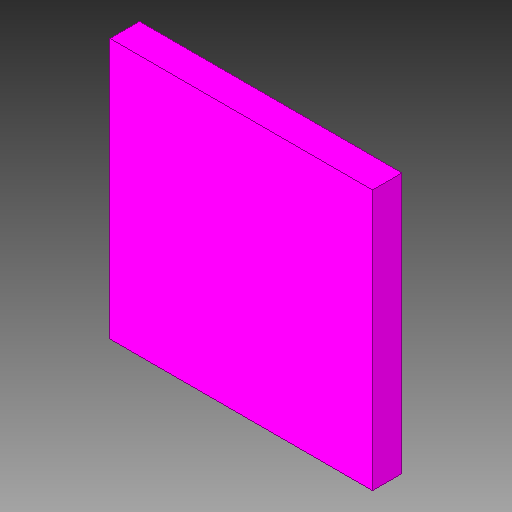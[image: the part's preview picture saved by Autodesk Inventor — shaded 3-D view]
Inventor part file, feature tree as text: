
AUTODESK INVENTOR PART (.ipt)
format: ipt  version: 2018 (Build 220112000, 112)  size: 80,896 bytes
history: native  units: in
note: dims shown in document units (in); Inventor stores cm internally (conversion verified against a paired STEP export)
features: other x1, extrude x1
ambient origin geometry x8: Origin, YZ Plane, XZ Plane, XY Plane, X Axis, Y Axis, Z Axis, Center Point
bodies: Solid1 (feature_tree)
feature tree (2):
  other  "RGC64, MSP430F5528IRGC_89"
  extrude  "Extrusion1"  Depth=0.0394in TaperAngle=0.0deg
